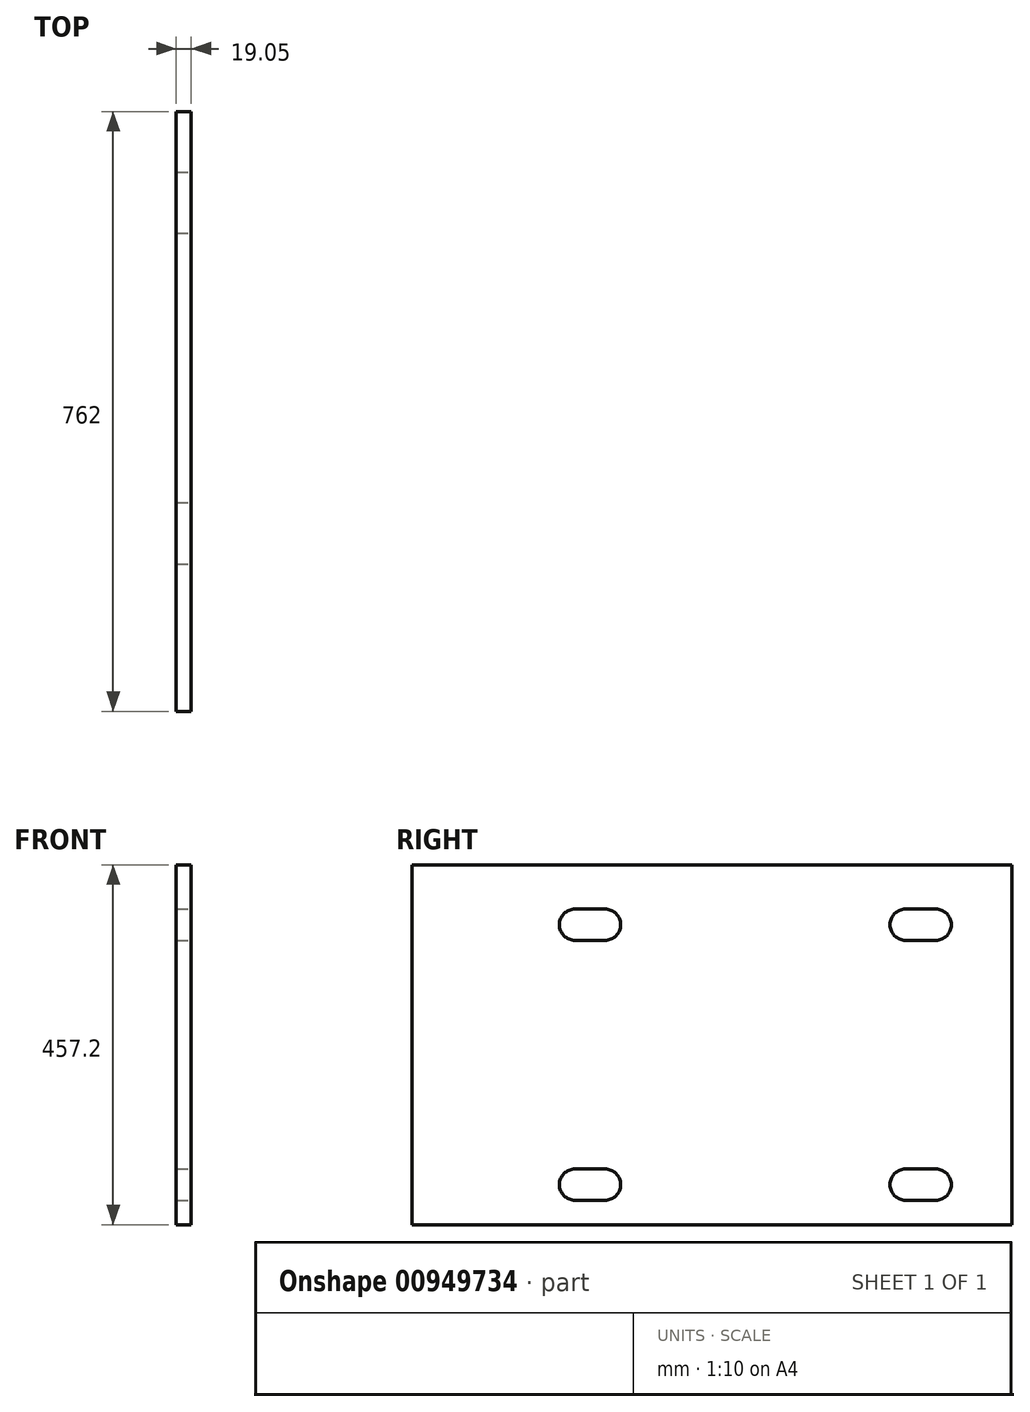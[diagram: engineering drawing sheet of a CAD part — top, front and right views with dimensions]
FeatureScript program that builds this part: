
annotation { "Feature Type Name" : "Feature", "Feature Type Description" : "" }
export const myFeature = defineFeature(function(context is Context, id is Id, definition is map)
    precondition{}
    {
        {
            var Q0;
            Q0=qCreatedBy(makeId("Front.planeOp"),FACE);
            var sketch = newSketch(context, id + "F0", { "sketchPlane" : qUnion([Q0])});
            skLineSegment(sketch, "E0", {"start": v(0, 228.6) * mm, "end": v(0, -228.6) * mm});
            skLineSegment(sketch, "E1", {"start": v(0, -228.6) * mm, "end": v(-19.05, -228.6) * mm});
            skLineSegment(sketch, "E2", {"start": v(0, 228.6) * mm, "end": v(-19.05, 228.6) * mm});
            skLineSegment(sketch, "E3", {"start": v(-19.05, 228.6) * mm, "end": v(-19.05, -228.6) * mm});
            skSolve(sketch);
        }
        {
            var Q0;
            Q0 = qSketchRegion(id + "F0", true);
            extrude(context, id + "F1", {"entities" : qUnion([Q0]), "endBound" : BoundingType.SYMMETRIC, "depth" : 762 * mm, "offsetDistance" : 25.4 * mm});
        }
        {
            var Q0;
            Q0=makeQuery(id+"F1.opExtrude","SWEPT_FACE",FACE,{"disambiguationData":[OSD([sQuery(id+"F0.wireOp",EDGE,"E0")])]});
            var sketch = newSketch(context, id + "F2", { "sketchPlane" : qUnion([Q0])});
            skLineSegment(sketch, "E4", {"start": v(-174.04, -177.8) * mm, "end": v(-155, -177.8) * mm});
            skLineSegment(sketch, "E5", {"start": v(245.95, -177.8) * mm, "end": v(265, -177.8) * mm});
            skLineSegment(sketch, "E6", {"start": v(-155, -177.8) * mm, "end": v(-135.94, -177.8) * mm});
            skLineSegment(sketch, "E7", {"start": v(265, -177.8) * mm, "end": v(284.05, -177.8) * mm});
            skArc(sketch, "E8.0.startCap", {"start": v(-174.04, -197.64) * mm, "mid": v(-193.88, -177.8) * mm, "end": v(-174.04, -157.96) * mm});
            skArc(sketch, "E8.0.endCap", {"start": v(-155, -157.96) * mm, "mid": v(-135.15, -177.8) * mm, "end": v(-155, -197.64) * mm});
            skLineSegment(sketch, "E8.0.left", {"start": v(-174.04, -157.96) * mm, "end": v(-155, -157.96) * mm});
            skLineSegment(sketch, "E8.0.right", {"start": v(-174.04, -197.64) * mm, "end": v(-155, -197.64) * mm});
            skArc(sketch, "E8.1.startCap", {"start": v(-155, -197.64) * mm, "mid": v(-174.83, -177.8) * mm, "end": v(-155, -157.96) * mm});
            skArc(sketch, "E8.1.endCap", {"start": v(-135.94, -157.96) * mm, "mid": v(-116.1, -177.8) * mm, "end": v(-135.94, -197.64) * mm});
            skLineSegment(sketch, "E8.1.left", {"start": v(-155, -157.96) * mm, "end": v(-135.94, -157.96) * mm});
            skLineSegment(sketch, "E8.1.right", {"start": v(-155, -197.64) * mm, "end": v(-135.94, -197.64) * mm});
            skArc(sketch, "E8.2.startCap", {"start": v(245.95, -197.64) * mm, "mid": v(226.1, -177.8) * mm, "end": v(245.95, -157.96) * mm});
            skArc(sketch, "E8.2.endCap", {"start": v(265, -157.96) * mm, "mid": v(284.84, -177.8) * mm, "end": v(265, -197.64) * mm});
            skLineSegment(sketch, "E8.2.left", {"start": v(245.95, -157.96) * mm, "end": v(265, -157.96) * mm});
            skLineSegment(sketch, "E8.2.right", {"start": v(245.95, -197.64) * mm, "end": v(265, -197.64) * mm});
            skArc(sketch, "E8.3.startCap", {"start": v(265, -197.64) * mm, "mid": v(245.15, -177.8) * mm, "end": v(265, -157.96) * mm});
            skArc(sketch, "E8.3.endCap", {"start": v(284.05, -157.96) * mm, "mid": v(303.9, -177.8) * mm, "end": v(284.05, -197.64) * mm});
            skLineSegment(sketch, "E8.3.left", {"start": v(265, -157.96) * mm, "end": v(284.05, -157.96) * mm});
            skLineSegment(sketch, "E8.3.right", {"start": v(265, -197.64) * mm, "end": v(284.05, -197.64) * mm});
            skArc(sketch, "E9.0.1.0", {"start": v(-174.04, 132.56) * mm, "mid": v(-193.88, 152.4) * mm, "end": v(-174.04, 172.24) * mm});
            skLineSegment(sketch, "E9.0.1.1", {"start": v(-174.04, 132.56) * mm, "end": v(-155, 132.56) * mm});
            skLineSegment(sketch, "E9.0.1.2", {"start": v(-174.04, 172.24) * mm, "end": v(-155, 172.24) * mm});
            skLineSegment(sketch, "E9.0.1.3", {"start": v(-155, 172.24) * mm, "end": v(-135.94, 172.24) * mm});
            skArc(sketch, "E9.0.1.4", {"start": v(-135.94, 172.24) * mm, "mid": v(-116.1, 152.4) * mm, "end": v(-135.94, 132.56) * mm});
            skLineSegment(sketch, "E9.0.1.5", {"start": v(-155, 132.56) * mm, "end": v(-135.94, 132.56) * mm});
            skArc(sketch, "E9.0.1.6", {"start": v(245.95, 132.56) * mm, "mid": v(226.1, 152.4) * mm, "end": v(245.95, 172.24) * mm});
            skArc(sketch, "E9.0.1.7", {"start": v(284.05, 172.24) * mm, "mid": v(303.9, 152.4) * mm, "end": v(284.05, 132.56) * mm});
            skLineSegment(sketch, "E9.0.1.8", {"start": v(245.95, 132.56) * mm, "end": v(265, 132.56) * mm});
            skLineSegment(sketch, "E9.0.1.9", {"start": v(265, 132.56) * mm, "end": v(284.05, 132.56) * mm});
            skLineSegment(sketch, "E9.0.1.10", {"start": v(265, 172.24) * mm, "end": v(284.05, 172.24) * mm});
            skLineSegment(sketch, "E9.0.1.11", {"start": v(245.95, 172.24) * mm, "end": v(265, 172.24) * mm});
            skLineSegment(sketch, "E9.direction1", {"start": v(-174.04, -197.64) * mm, "end": v(-148.64, -197.64) * mm, "construction": true});
            skLineSegment(sketch, "E9.direction2", {"start": v(-174.04, -197.64) * mm, "end": v(-174.04, 132.56) * mm, "construction": true});
            skSolve(sketch);
        }
        {
            var Q0;
            Q0 = qSketchRegion(id + "F2", true);
            extrude(context, id + "F3", {"entities" : qUnion([Q0]), "operationType" : NewBodyOperationType.REMOVE, "endBound" : BoundingType.THROUGH_ALL, "oppositeDirection" : true, "depth" : 25.4 * mm, "offsetDistance" : 25.4 * mm});
        }
    });
